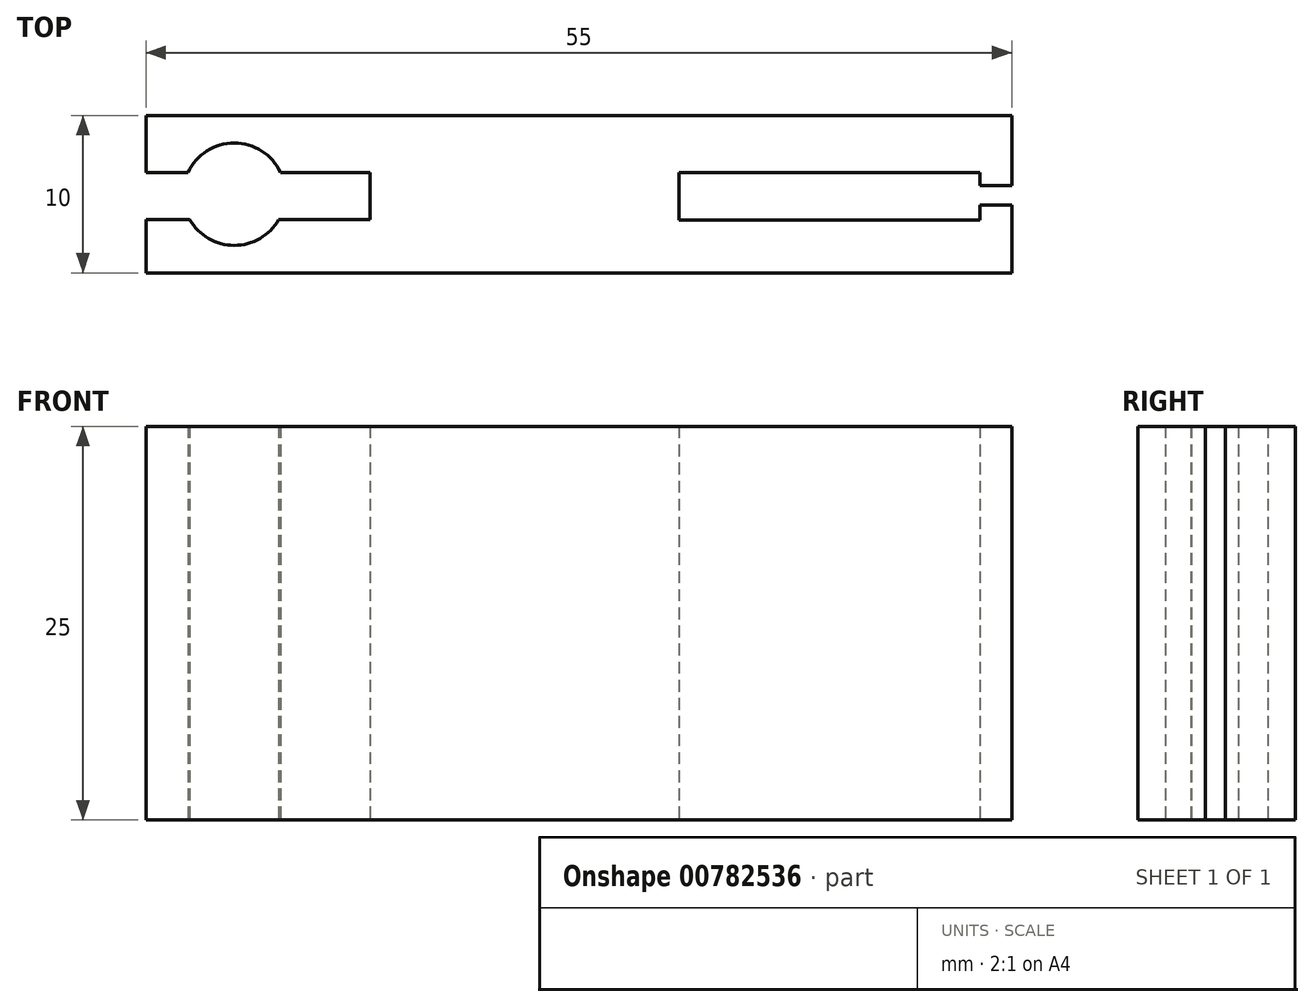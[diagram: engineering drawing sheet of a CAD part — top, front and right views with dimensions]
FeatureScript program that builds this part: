
annotation { "Feature Type Name" : "Feature", "Feature Type Description" : "" }
export const myFeature = defineFeature(function(context is Context, id is Id, definition is map)
    precondition{}
    {
        {
            var Q0;
            Q0=qCreatedBy(makeId("Top.planeOp"),FACE);
            var sketch = newSketch(context, id + "F0", { "sketchPlane" : qUnion([Q0])});
            skLineSegment(sketch, "E0.bottom", {"start": v(0, 0) * mm, "end": v(55, 0) * mm});
            skLineSegment(sketch, "E0.top", {"start": v(0, 10) * mm, "end": v(55, 10) * mm});
            skLineSegment(sketch, "E0.right", {"start": v(55, 0) * mm, "end": v(55, 4.3) * mm});
            skArc(sketch, "E1", {"start": v(8.55, 6.39) * mm, "mid": v(5.61, 8.25) * mm, "end": v(2.67, 6.39) * mm});
            skLineSegment(sketch, "E2.bottom", {"start": v(0, 6.39) * mm, "end": v(2.67, 6.39) * mm});
            skLineSegment(sketch, "E2.top", {"start": v(0, 3.39) * mm, "end": v(2.79, 3.39) * mm});
            skLineSegment(sketch, "E2.right", {"start": v(14.24, 6.39) * mm, "end": v(14.24, 3.39) * mm});
            skLineSegment(sketch, "E3", {"start": v(0, 10) * mm, "end": v(0, 6.39) * mm});
            skLineSegment(sketch, "E4", {"start": v(0, 0) * mm, "end": v(0, 3.39) * mm});
            skArc(sketch, "E5.trimOffspring", {"start": v(2.79, 3.39) * mm, "mid": v(5.61, 1.75) * mm, "end": v(8.43, 3.39) * mm});
            skLineSegment(sketch, "E6.trimOffspring", {"start": v(8.55, 6.39) * mm, "end": v(14.24, 6.39) * mm});
            skLineSegment(sketch, "E7.trimOffspring", {"start": v(8.43, 3.39) * mm, "end": v(14.24, 3.39) * mm});
            skLineSegment(sketch, "E8.bottom", {"start": v(33.84, 6.39) * mm, "end": v(52.96, 6.39) * mm});
            skLineSegment(sketch, "E8.top", {"start": v(33.84, 3.37) * mm, "end": v(52.96, 3.37) * mm});
            skLineSegment(sketch, "E8.left", {"start": v(33.84, 6.39) * mm, "end": v(33.84, 3.37) * mm});
            skLineSegment(sketch, "E8.right", {"start": v(52.96, 6.39) * mm, "end": v(52.96, 5.55) * mm});
            skLineSegment(sketch, "E9.bottom", {"start": v(52.96, 5.55) * mm, "end": v(55, 5.55) * mm});
            skLineSegment(sketch, "E9.top", {"start": v(52.96, 4.3) * mm, "end": v(55, 4.3) * mm});
            skLineSegment(sketch, "E10.trimOffspring", {"start": v(52.96, 4.3) * mm, "end": v(52.96, 3.37) * mm});
            skLineSegment(sketch, "E11.trimOffspring", {"start": v(55, 5.55) * mm, "end": v(55, 10) * mm});
            skSolve(sketch);
        }
        {
            var Q0;
            Q0 = qSketchRegion(id + "F0", true);
            extrude(context, id + "F1", {"entities" : qUnion([Q0]), "depth" : 25 * mm, "offsetDistance" : 25 * mm});
        }
    });
